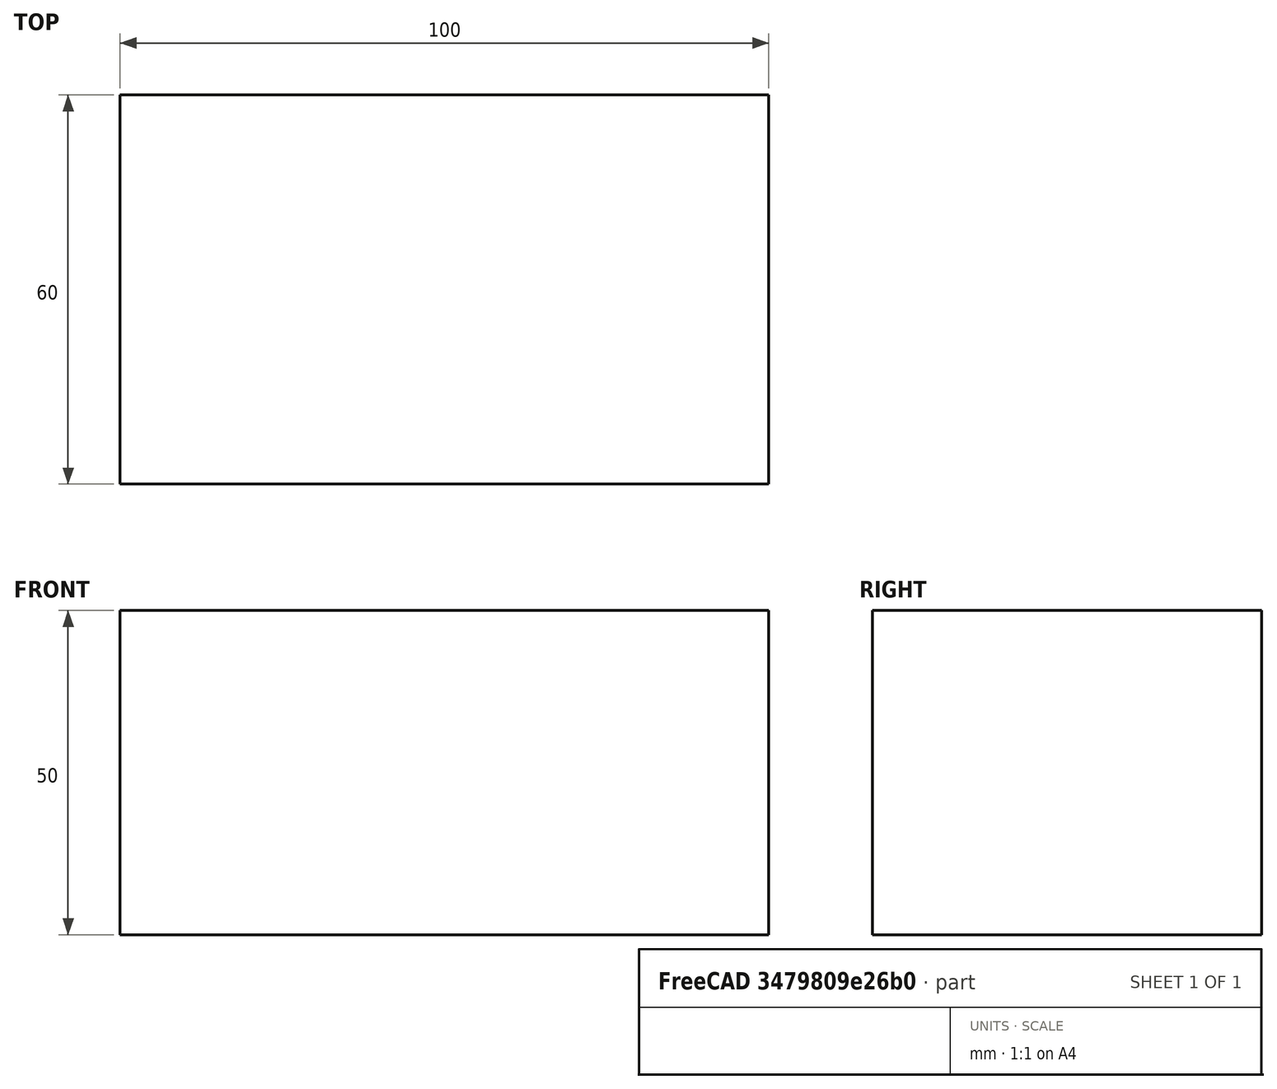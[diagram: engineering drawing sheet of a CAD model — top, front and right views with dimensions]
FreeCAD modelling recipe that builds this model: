
FCSTD DOCUMENT  (FreeCAD 0.15R4671 (Git))
Label: Flat Bar 100x60 EN10058 S235JR
License: All rights reserved
LicenseURL: http://en.wikipedia.org/wiki/All_rights_reserved
objects: Sketcher::SketchObject×1, Part::Extrusion×1
note: 2 computed .brp shape members not serialized (recipe doc carries the construction recipe); baked Part::Feature solids carry a one-line shape summary decoded from their .brp

FEATURE [Sketcher::SketchObject] Sketch
  sketch-geometry (4):
    g0: LineSegment StartX=-50 StartY=-30 StartZ=0 EndX=50 EndY=-30 EndZ=0
    g1: LineSegment StartX=50 StartY=-30 StartZ=0 EndX=50 EndY=30 EndZ=0
    g2: LineSegment StartX=50 StartY=30 StartZ=0 EndX=-50 EndY=30 EndZ=0
    g3: LineSegment StartX=-50 StartY=30 StartZ=0 EndX=-50 EndY=-30 EndZ=0
  constraints (12):
    c: Coincident(g0,g1)
    c: Coincident(g1,g2)
    c: Coincident(g2,g3)
    c: Coincident(g3,g0)
    c: Horizontal(g0)
    c: Horizontal(g2)
    c: Vertical(g1)
    c: Vertical(g3)
    c: Symmetric(g1,g2,g-2)
    c: Symmetric(g0,g1,g-1)
    c: DistanceY(g1) = 60
    c: DistanceX(g0) = 100
FEATURE [Part::Extrusion] Extrude  label="Flat Bar 100x60 EN10058 S235JR"
  Base = -> Sketch
  Dir = (0,0,50)
  Solid = true
